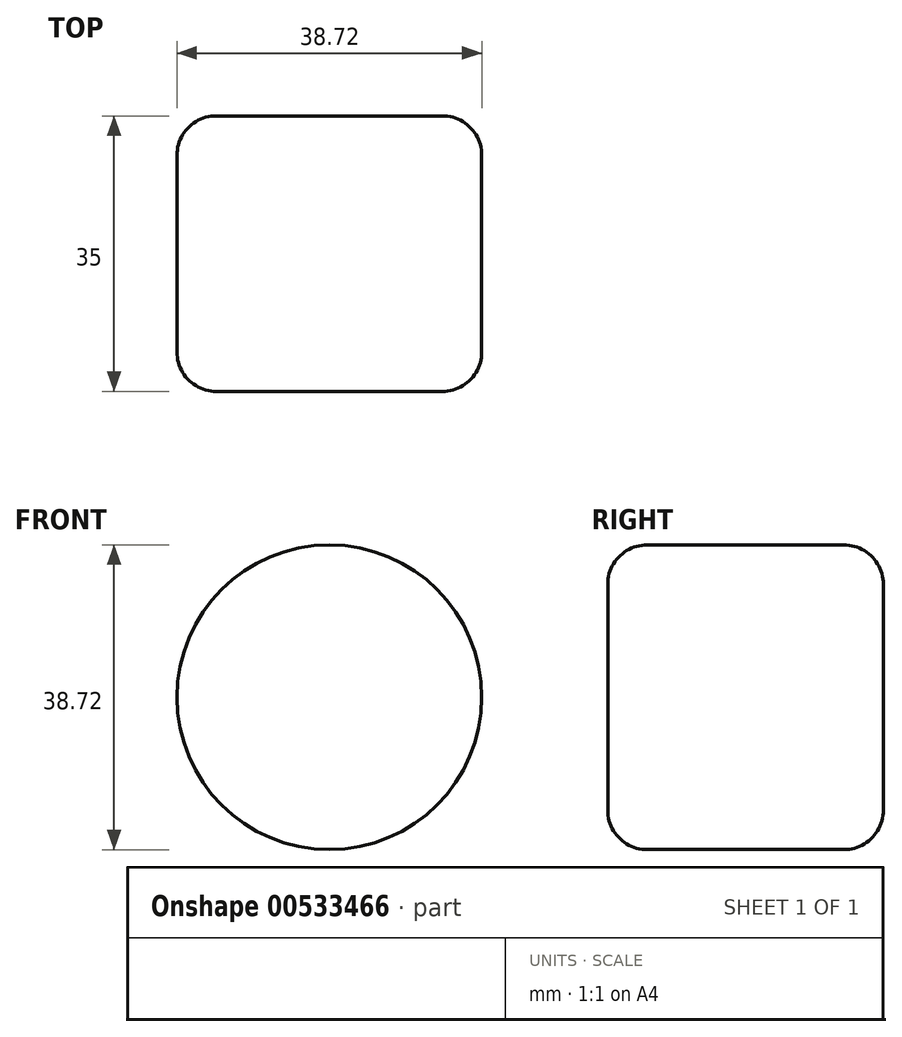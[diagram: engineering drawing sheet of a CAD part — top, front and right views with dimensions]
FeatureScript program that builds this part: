
annotation { "Feature Type Name" : "Feature", "Feature Type Description" : "" }
export const myFeature = defineFeature(function(context is Context, id is Id, definition is map)
    precondition{}
    {
        {
            var Q0;
            Q0=qCreatedBy(makeId("Front.planeOp"),FACE);
            var sketch = newSketch(context, id + "F0", { "sketchPlane" : qUnion([Q0])});
            skCircle(sketch, "E0", {"center": v(0, 0) * mm, "radius": 19.36 * mm});
            skSolve(sketch);
        }
        {
            var Q0;
            Q0=makeQuery(id+"F0.imprint","IMPRINT",FACE,{"disambiguationData":[TD([[makeQuery(id+"F0.imprint","IMPRINT",EDGE,{"derivedFrom":sQuery(id+"F0.wireOp",EDGE,"E0")}),1.0]])]});
            extrude(context, id + "F1", {"entities" : qUnion([Q0]), "endBound" : BoundingType.SYMMETRIC, "depth" : 35 * mm, "offsetDistance" : 25 * mm});
        }
        {
            var Q0;
            Q0=makeQuery(id+"F1.opExtrude","CAP_EDGE",EDGE,{"disambiguationData":[OSD([sQuery(id+"F0.wireOp",EDGE,"E0")])],"isStart":false});
            fillet(context, id + "F2", {"entities" : qUnion([Q0]), "radius" : 5 * mm, "tangentPropagation" : true, "allowEdgeOverflow" : false});
        }
        {
            var Q0;
            Q0=makeQuery(id+"F1.opExtrude","CAP_EDGE",EDGE,{"disambiguationData":[OSD([sQuery(id+"F0.wireOp",EDGE,"E0")])],"isStart":true});
            fillet(context, id + "F3", {"entities" : qUnion([Q0]), "radius" : 5 * mm, "tangentPropagation" : true, "allowEdgeOverflow" : false});
        }
    });
